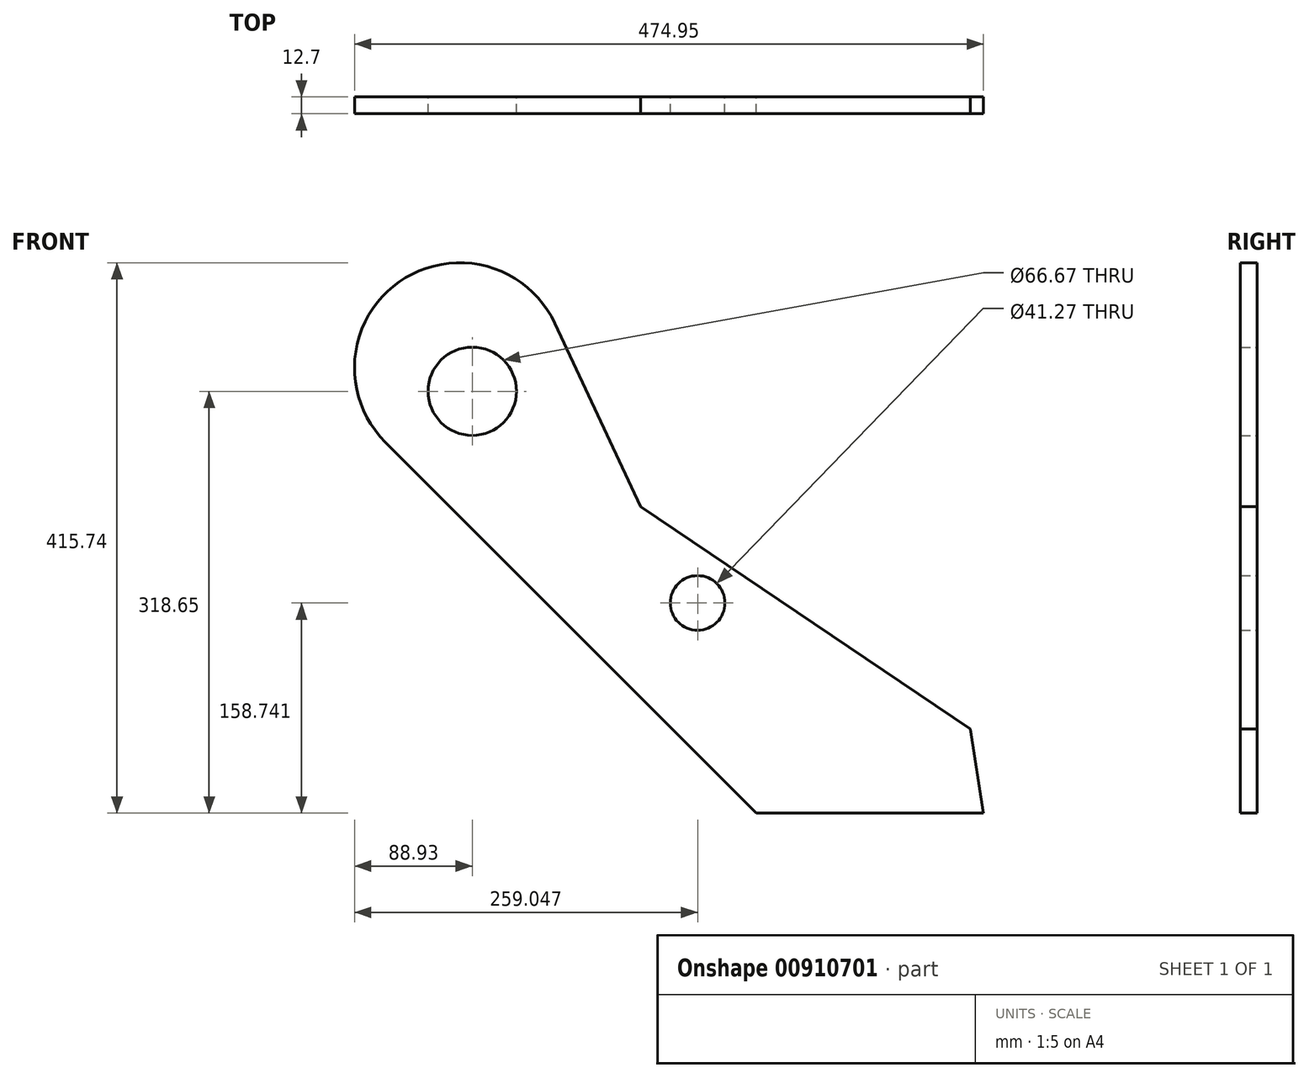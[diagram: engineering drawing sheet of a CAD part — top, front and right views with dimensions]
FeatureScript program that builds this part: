
annotation { "Feature Type Name" : "Feature", "Feature Type Description" : "" }
export const myFeature = defineFeature(function(context is Context, id is Id, definition is map)
    precondition{}
    {
        {
            var Q0;
            Q0=qCreatedBy(makeId("Front.planeOp"),FACE);
            var sketch = newSketch(context, id + "F0", { "sketchPlane" : qUnion([Q0])});
            skCircle(sketch, "E0", {"center": v(0, 0) * mm, "radius": 33.34 * mm});
            skArc(sketch, "E1", {"start": v(62.39, 51.26) * mm, "mid": v(-55.08, 82.74) * mm, "end": v(-65.68, -38.41) * mm});
            skLineSegment(sketch, "E2", {"start": v(-65.68, -38.41) * mm, "end": v(214.57, -318.65) * mm});
            skLineSegment(sketch, "E3", {"start": v(214.57, -318.65) * mm, "end": v(386.02, -318.65) * mm});
            skLineSegment(sketch, "E4", {"start": v(386.02, -318.65) * mm, "end": v(375.97, -255.23) * mm});
            skLineSegment(sketch, "E5", {"start": v(375.97, -255.23) * mm, "end": v(127, -87.3) * mm});
            skLineSegment(sketch, "E6", {"start": v(127, -87.3) * mm, "end": v(62.39, 51.26) * mm});
            skCircle(sketch, "E7", {"center": v(170.12, -159.9) * mm, "radius": 20.64 * mm});
            skSolve(sketch);
        }
        {
            var Q0;
            Q0=makeQuery(id+"F0.imprint","IMPRINT",FACE,{"disambiguationData":[TD([[makeQuery(id+"F0.imprint","IMPRINT",EDGE,{"derivedFrom":sQuery(id+"F0.wireOp",EDGE,"E0")}),-1.0]])]});
            extrude(context, id + "F1", {"entities" : qUnion([Q0]), "depth" : 12.7 * mm, "offsetDistance" : 25.4 * mm});
        }
    });
